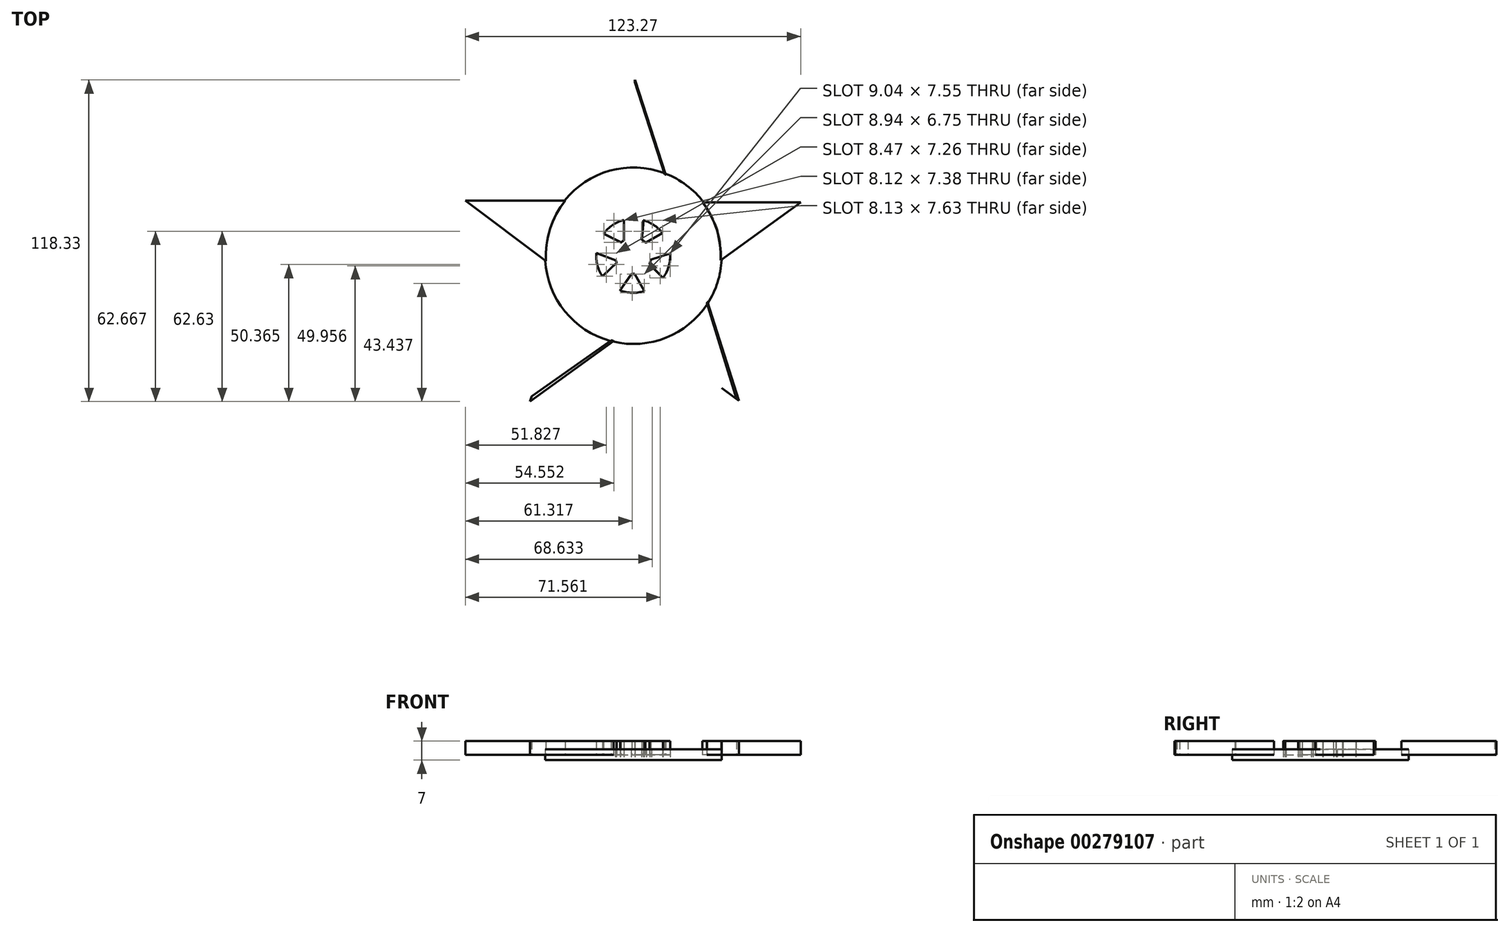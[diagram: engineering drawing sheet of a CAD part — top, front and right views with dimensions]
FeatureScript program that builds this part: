
annotation { "Feature Type Name" : "Feature", "Feature Type Description" : "" }
export const myFeature = defineFeature(function(context is Context, id is Id, definition is map)
    precondition{}
    {
        {
            var Q0;
            Q0=qCreatedBy(makeId("Top.planeOp"),FACE);
            var sketch = newSketch(context, id + "F0", { "sketchPlane" : qUnion([Q0])});
            skLineSegment(sketch, "E0", {"start": v(-59.08, 13.14) * mm, "end": v(-22.33, 13.14) * mm});
            skLineSegment(sketch, "E1", {"start": v(-59.08, 13.14) * mm, "end": v(-29.47, -9.06) * mm});
            skCircle(sketch, "E2", {"center": v(2.62, -7.12) * mm, "radius": 32.15 * mm});
            skLineSegment(sketch, "E3", {"start": v(65.07, 12.56) * mm, "end": v(28.04, 12.56) * mm});
            skLineSegment(sketch, "E4", {"start": v(65.07, 12.56) * mm, "end": v(34.67, -9.69) * mm});
            skLineSegment(sketch, "E5", {"start": v(14.59, 22.72) * mm, "end": v(3.3, 57.6) * mm});
            skLineSegment(sketch, "E6", {"start": v(3.3, 57.6) * mm, "end": v(-7.94, 23.24) * mm});
            skLineSegment(sketch, "E7", {"start": v(41.47, -60.47) * mm, "end": v(29.9, -24.14) * mm});
            skLineSegment(sketch, "E8", {"start": v(41.47, -60.47) * mm, "end": v(11.18, -38.11) * mm});
            skLineSegment(sketch, "E9", {"start": v(-35.35, -60.73) * mm, "end": v(-4.56, -38.46) * mm});
            skLineSegment(sketch, "E10", {"start": v(-35.35, -60.73) * mm, "end": v(-23.82, -25.4) * mm});
            skCircle(sketch, "E11", {"center": v(2.62, -7.12) * mm, "radius": 17.17 * mm});
            skCircle(sketch, "E12", {"center": v(2.62, -7.12) * mm, "radius": 13.62 * mm});
            skCircle(sketch, "E13", {"center": v(2.62, -7.12) * mm, "radius": 6.6 * mm});
            skLineSegment(sketch, "E14", {"start": v(-0.77, 6.06) * mm, "end": v(-0.77, -1.46) * mm});
            skLineSegment(sketch, "E15", {"start": v(6.43, 5.95) * mm, "end": v(5.78, -1.32) * mm});
            skLineSegment(sketch, "E16", {"start": v(13.35, 1.26) * mm, "end": v(7.1, -2.27) * mm});
            skLineSegment(sketch, "E17", {"start": v(16.21, -6.23) * mm, "end": v(9.08, -8.5) * mm});
            skLineSegment(sketch, "E18", {"start": v(-8.27, 1.05) * mm, "end": v(-1.81, -2.23) * mm});
            skLineSegment(sketch, "E19", {"start": v(-10.96, -6.1) * mm, "end": v(-3.78, -8.74) * mm});
            skLineSegment(sketch, "E20", {"start": v(13.53, -15.28) * mm, "end": v(8.54, -10.06) * mm});
            skLineSegment(sketch, "E21", {"start": v(6.7, -20.12) * mm, "end": v(3.14, -13.7) * mm});
            skLineSegment(sketch, "E22", {"start": v(-2.22, -19.86) * mm, "end": v(2.1, -13.7) * mm});
            skLineSegment(sketch, "E23", {"start": v(-8.73, -14.65) * mm, "end": v(-3.48, -9.66) * mm});
            skLineSegment(sketch, "E24.1.0", {"start": v(-35.72, -59.54) * mm, "end": v(-24.36, -24.6) * mm});
            skLineSegment(sketch, "E24.1.1", {"start": v(-35.72, -59.54) * mm, "end": v(-5.45, -38.24) * mm});
            skLineSegment(sketch, "E24.2.0", {"start": v(40.63, -59.79) * mm, "end": v(10.9, -38.19) * mm});
            skLineSegment(sketch, "E24.2.1", {"start": v(40.63, -59.79) * mm, "end": v(29.72, -24.42) * mm});
            skLineSegment(sketch, "E24.3.0", {"start": v(64.45, 12.75) * mm, "end": v(34.73, -8.85) * mm});
            skLineSegment(sketch, "E24.3.1", {"start": v(64.45, 12.75) * mm, "end": v(27.45, 13.3) * mm});
            skLineSegment(sketch, "E24.4.0", {"start": v(2.83, 57.82) * mm, "end": v(14.18, 22.87) * mm});
            skLineSegment(sketch, "E24.4.1", {"start": v(2.83, 57.82) * mm, "end": v(-9.13, 22.8) * mm});
            skSolve(sketch);
        }
        {
            var Q0;
            {var subQ0=sQuery(id+"F0.wireOp",EDGE,"E5");Q0=makeQuery(id+"F0.imprint","IMPRINT",FACE,{"disambiguationData":[TD([[makeQuery(id+"F0.imprint","IMPRINT",EDGE,{"derivedFrom":subQ0}),1.0]])]});}
            var Q1;
            {var subQ0=sQuery(id+"F0.wireOp",EDGE,"E0");Q1=makeQuery(id+"F0.imprint","IMPRINT",FACE,{"disambiguationData":[TD([[makeQuery(id+"F0.imprint","IMPRINT",EDGE,{"derivedFrom":subQ0}),-1.0]])]});}
            var Q2;
            {var subQ0=sQuery(id+"F0.wireOp",EDGE,"E3");Q2=makeQuery(id+"F0.imprint","IMPRINT",FACE,{"disambiguationData":[TD([[makeQuery(id+"F0.imprint","IMPRINT",EDGE,{"derivedFrom":subQ0}),1.0]])]});}
            var Q3;
            {var subQ0=sQuery(id+"F0.wireOp",EDGE,"E9");Q3=makeQuery(id+"F0.imprint","IMPRINT",FACE,{"disambiguationData":[TD([[makeQuery(id+"F0.imprint","IMPRINT",EDGE,{"derivedFrom":subQ0}),1.0]])]});}
            var Q4;
            {var subQ0=sQuery(id+"F0.wireOp",EDGE,"E7");Q4=makeQuery(id+"F0.imprint","IMPRINT",FACE,{"disambiguationData":[TD([[makeQuery(id+"F0.imprint","IMPRINT",EDGE,{"derivedFrom":subQ0}),1.0]])]});}
            var Q5;
            {var subQ0=sQuery(id+"F0.wireOp",EDGE,"E15");Q5=makeQuery(id+"F0.imprint","IMPRINT",FACE,{"disambiguationData":[TD([[makeQuery(id+"F0.imprint","IMPRINT",EDGE,{"derivedFrom":subQ0}),1.0]])]});}
            var Q6;
            {var subQ0=sQuery(id+"F0.wireOp",EDGE,"E14");Q6=makeQuery(id+"F0.imprint","IMPRINT",FACE,{"disambiguationData":[TD([[makeQuery(id+"F0.imprint","IMPRINT",EDGE,{"derivedFrom":subQ0}),-1.0]])]});}
            var Q7;
            {var subQ0=sQuery(id+"F0.wireOp",EDGE,"E19");Q7=makeQuery(id+"F0.imprint","IMPRINT",FACE,{"disambiguationData":[TD([[makeQuery(id+"F0.imprint","IMPRINT",EDGE,{"derivedFrom":subQ0}),-1.0]])]});}
            var Q8;
            {var subQ0=sQuery(id+"F0.wireOp",EDGE,"E21");Q8=makeQuery(id+"F0.imprint","IMPRINT",FACE,{"disambiguationData":[TD([[makeQuery(id+"F0.imprint","IMPRINT",EDGE,{"derivedFrom":subQ0}),1.0]])]});}
            var Q9;
            {var subQ0=sQuery(id+"F0.wireOp",EDGE,"E17");Q9=makeQuery(id+"F0.imprint","IMPRINT",FACE,{"disambiguationData":[TD([[makeQuery(id+"F0.imprint","IMPRINT",EDGE,{"derivedFrom":subQ0}),1.0]])]});}
            extrude(context, id + "F1", {"entities" : qUnion([Q0, Q1, Q2, Q3, Q4, Q5, Q6, Q7, Q8, Q9]), "depth" : 5 * mm});
        }
        {
            var Q0;
            Q0=qCreatedBy(makeId("Top.planeOp"),FACE);
            var sketch = newSketch(context, id + "F2", { "sketchPlane" : qUnion([Q0])});
            skCircle(sketch, "E25", {"center": v(2.69, -7.1) * mm, "radius": 32.46 * mm});
            skCircle(sketch, "E26", {"center": v(2.69, -7.1) * mm, "radius": 6.86 * mm});
            skCircle(sketch, "E27", {"center": v(2.69, -7.1) * mm, "radius": 13.57 * mm});
            skLineSegment(sketch, "E28", {"start": v(-2.02, -2.13) * mm, "end": v(-8.22, 0.97) * mm});
            skLineSegment(sketch, "E29", {"start": v(-3.99, -8.67) * mm, "end": v(-10.85, -6.13) * mm});
            skLineSegment(sketch, "E30", {"start": v(-3.62, -9.78) * mm, "end": v(-8.63, -14.6) * mm});
            skLineSegment(sketch, "E31", {"start": v(1.91, -13.92) * mm, "end": v(-2.23, -19.75) * mm});
            skLineSegment(sketch, "E32", {"start": v(3.32, -13.93) * mm, "end": v(6.7, -20.07) * mm});
            skLineSegment(sketch, "E33", {"start": v(8.7, -10.39) * mm, "end": v(13.5, -15.3) * mm});
            skLineSegment(sketch, "E34", {"start": v(9.41, -8.44) * mm, "end": v(16.23, -6.25) * mm});
            skLineSegment(sketch, "E35", {"start": v(7.44, -2.17) * mm, "end": v(13.37, 1.27) * mm});
            skLineSegment(sketch, "E36", {"start": v(5.74, -0.97) * mm, "end": v(6.34, 5.96) * mm});
            skLineSegment(sketch, "E37", {"start": v(-0.84, -1.23) * mm, "end": v(-0.84, 6) * mm});
            skSolve(sketch);
        }
        {
            var Q0;
            Q0=makeQuery(id+"F2.imprint","IMPRINT",FACE,{"disambiguationData":[TD([[makeQuery(id+"F2.imprint","IMPRINT",EDGE,{"derivedFrom":sQuery(id+"F2.wireOp",EDGE,"E25")}),1.0]])]});
            var Q1;
            {var subQ0=sQuery(id+"F2.wireOp",EDGE,"E28");Q1=makeQuery(id+"F2.imprint","IMPRINT",FACE,{"disambiguationData":[TD([[makeQuery(id+"F2.imprint","IMPRINT",EDGE,{"derivedFrom":subQ0}),1.0]])]});}
            var Q2;
            {var subQ0=sQuery(id+"F2.wireOp",EDGE,"E36");Q2=makeQuery(id+"F2.imprint","IMPRINT",FACE,{"disambiguationData":[TD([[makeQuery(id+"F2.imprint","IMPRINT",EDGE,{"derivedFrom":subQ0}),1.0]])]});}
            var Q3;
            {var subQ0=sQuery(id+"F2.wireOp",EDGE,"E34");Q3=makeQuery(id+"F2.imprint","IMPRINT",FACE,{"disambiguationData":[TD([[makeQuery(id+"F2.imprint","IMPRINT",EDGE,{"derivedFrom":subQ0}),1.0]])]});}
            var Q4;
            {var subQ0=sQuery(id+"F2.wireOp",EDGE,"E26");var subQ5=makeQuery(id+"F2.imprint","INTERSECT",VERTEX,{"derivedFrom":[subQ0,sQuery(id+"F2.wireOp",EDGE,"E35")]});Q4=makeQuery(id+"F2.imprint","IMPRINT",FACE,{"disambiguationData":[TD([[makeQuery(id+"F2.imprint","IMPRINT",EDGE,{"disambiguationData":[TD([[subQ5,-1.0]])],"derivedFrom":subQ0}),1.0]])]});}
            var Q5;
            {var subQ0=sQuery(id+"F2.wireOp",EDGE,"E32");Q5=makeQuery(id+"F2.imprint","IMPRINT",FACE,{"disambiguationData":[TD([[makeQuery(id+"F2.imprint","IMPRINT",EDGE,{"derivedFrom":subQ0}),1.0]])]});}
            var Q6;
            {var subQ0=sQuery(id+"F2.wireOp",EDGE,"E30");Q6=makeQuery(id+"F2.imprint","IMPRINT",FACE,{"disambiguationData":[TD([[makeQuery(id+"F2.imprint","IMPRINT",EDGE,{"derivedFrom":subQ0}),1.0]])]});}
            extrude(context, id + "F3", {"entities" : qUnion([Q0, Q1, Q2, Q3, Q4, Q5, Q6]), "endBound" : BoundingType.SYMMETRIC, "depth" : 4 * mm});
        }
    });
